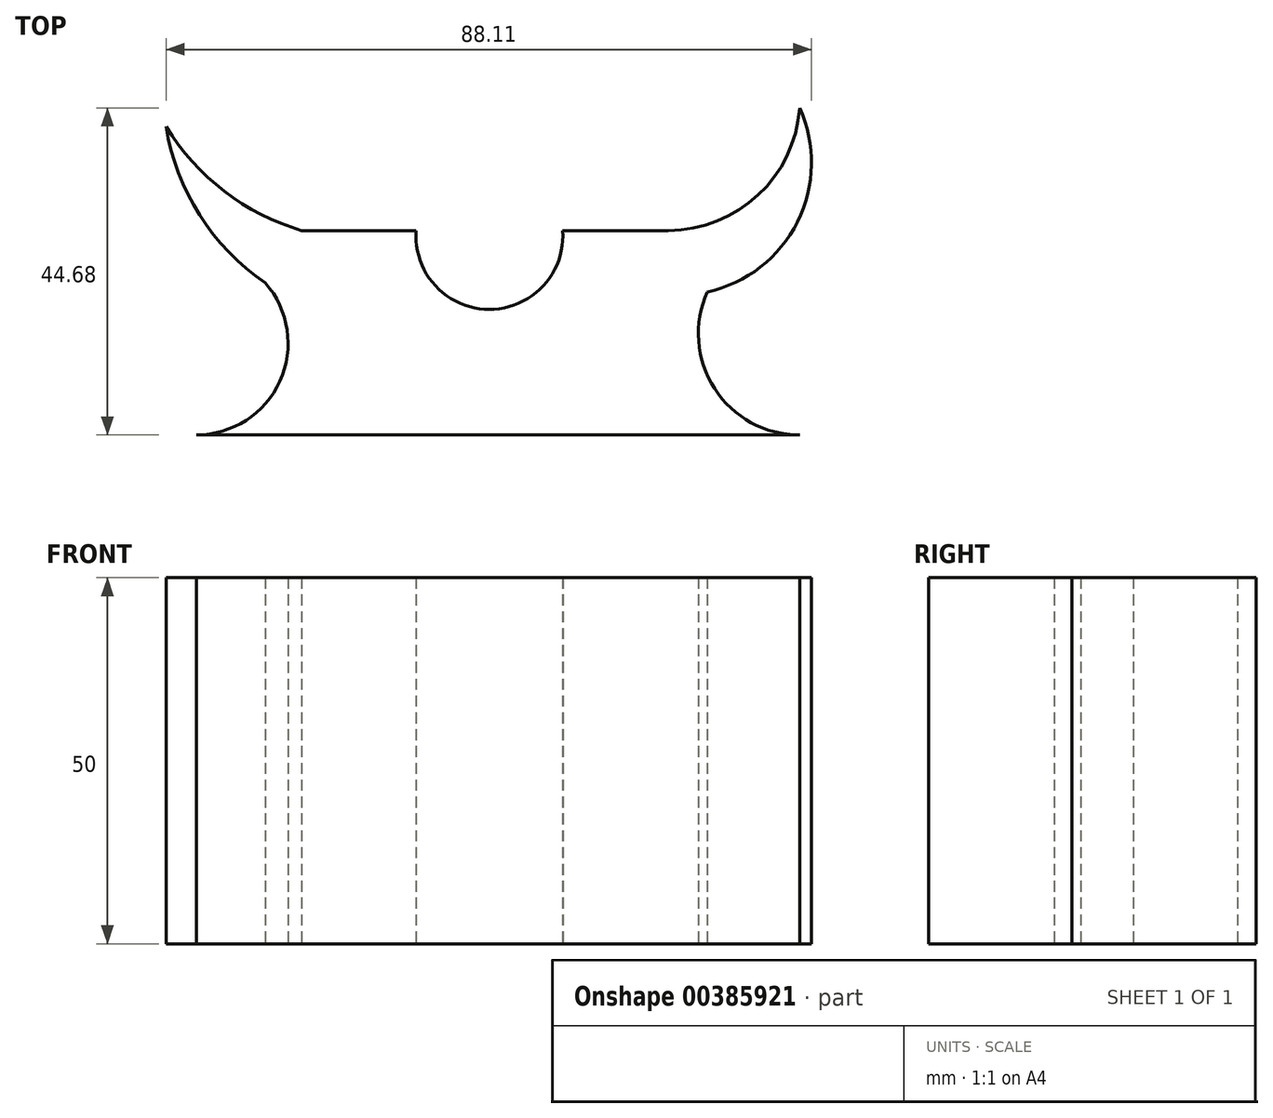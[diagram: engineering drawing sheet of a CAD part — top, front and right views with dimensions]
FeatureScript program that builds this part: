
annotation { "Feature Type Name" : "Feature", "Feature Type Description" : "" }
export const myFeature = defineFeature(function(context is Context, id is Id, definition is map)
    precondition{}
    {
        {
            var Q0;
            Q0=qCreatedBy(makeId("Top.planeOp"),FACE);
            var sketch = newSketch(context, id + "F0", { "sketchPlane" : qUnion([Q0])});
            skLineSegment(sketch, "E0", {"start": v(-43.08, 0) * mm, "end": v(-24.25, 0) * mm});
            skPoint(sketch, "E1.endSnap0", {"position": v(-33.67, 0) * mm});
            skArc(sketch, "E2", {"start": v(-47.23, 42.12) * mm, "mid": v(-42.65, 30.04) * mm, "end": v(-33.67, 20.74) * mm});
            skArc(sketch, "E3", {"start": v(-47.23, 42.12) * mm, "mid": v(-39.29, 33.29) * mm, "end": v(-28.7, 27.9) * mm});
            skArc(sketch, "E4", {"start": v(-43.08, 0) * mm, "mid": v(-31.7, 7.34) * mm, "end": v(-33.67, 20.74) * mm});
            skArc(sketch, "E5", {"start": v(64.53, 158.77) * mm, "mid": v(73.72, 166.3) * mm, "end": v(79.58, 176.62) * mm});
            skArc(sketch, "E6", {"start": v(21.3, 27.9) * mm, "mid": v(33.58, 32.75) * mm, "end": v(39.25, 44.68) * mm});
            skLineSegment(sketch, "E7", {"start": v(-24.25, 0) * mm, "end": v(39.25, 0) * mm});
            skArc(sketch, "E8", {"start": v(26.67, 19.53) * mm, "mid": v(38.97, 29.1) * mm, "end": v(39.25, 44.68) * mm});
            skArc(sketch, "E9", {"start": v(26.67, 19.53) * mm, "mid": v(27.64, 6.33) * mm, "end": v(39.25, 0) * mm});
            skArc(sketch, "E10", {"start": v(-13.1, 27.9) * mm, "mid": v(-3.1, 17.15) * mm, "end": v(6.9, 27.9) * mm});
            skLineSegment(sketch, "E11", {"start": v(-28.7, 27.9) * mm, "end": v(-13.1, 27.9) * mm});
            skLineSegment(sketch, "E12", {"start": v(6.9, 27.9) * mm, "end": v(21.3, 27.9) * mm});
            skSolve(sketch);
        }
        {
            var Q0;
            Q0 = qSketchRegion(id + "F0", true);
            extrude(context, id + "F1", {"entities" : qUnion([Q0]), "depth" : 50 * mm});
        }
    });
